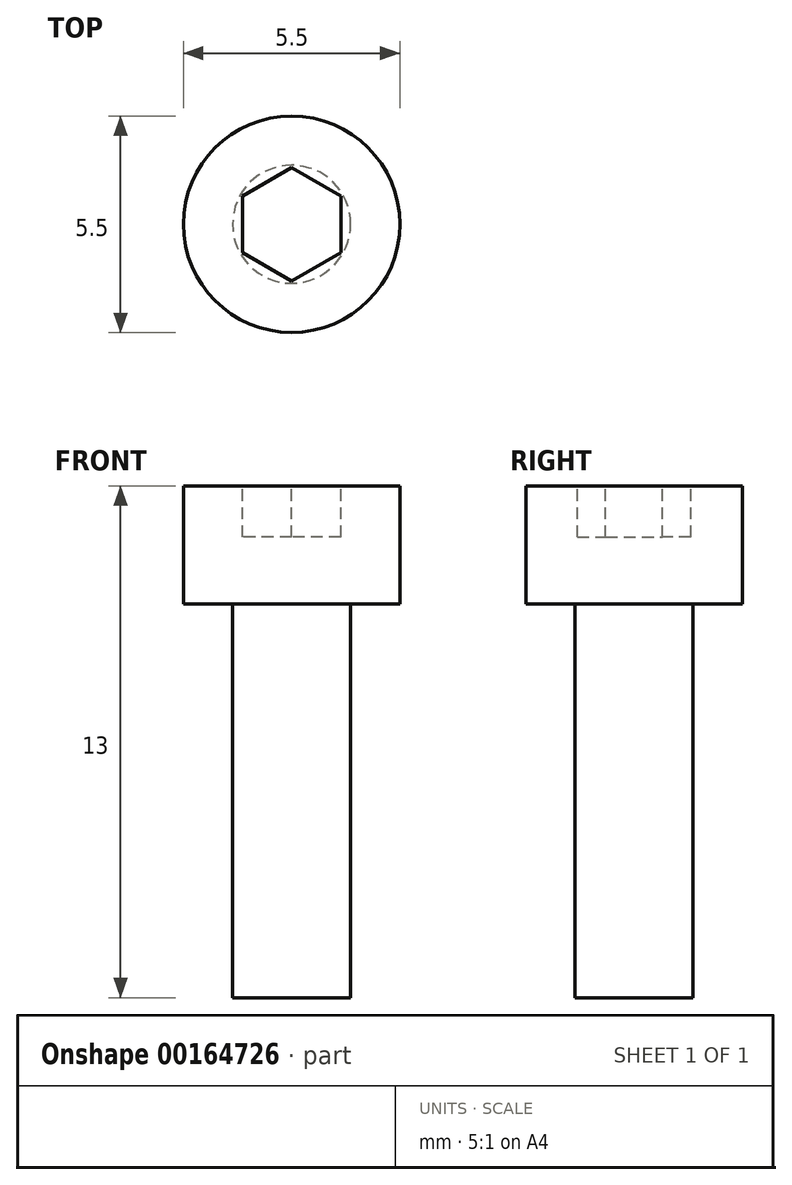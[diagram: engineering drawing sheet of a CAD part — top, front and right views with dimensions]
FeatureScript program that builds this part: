
annotation { "Feature Type Name" : "Feature", "Feature Type Description" : "" }
export const myFeature = defineFeature(function(context is Context, id is Id, definition is map)
    precondition{}
    {
        {
            var Q0;
            Q0=qCreatedBy(makeId("Front.planeOp"),FACE);
            var sketch = newSketch(context, id + "F0", { "sketchPlane" : qUnion([Q0])});
            skLineSegment(sketch, "E0", {"start": v(-1.5, 0) * mm, "end": v(-2.75, 0) * mm});
            skLineSegment(sketch, "E1", {"start": v(-2.75, 0) * mm, "end": v(-2.75, 3) * mm});
            skLineSegment(sketch, "E2", {"start": v(-2.75, 3) * mm, "end": v(0, 3) * mm});
            skLineSegment(sketch, "E3", {"start": v(0, 3) * mm, "end": v(0, 0) * mm});
            skLineSegment(sketch, "E4", {"start": v(-1.5, 0) * mm, "end": v(-1.5, -10) * mm});
            skLineSegment(sketch, "E5", {"start": v(-1.5, -10) * mm, "end": v(0, -10) * mm});
            skLineSegment(sketch, "E6", {"start": v(0, -10) * mm, "end": v(0, 0) * mm});
            skLineSegment(sketch, "E7", {"start": v(0, 3) * mm, "end": v(0, 8.62) * mm, "construction": true});
            skSolve(sketch);
        }
        {
            var Q0;
            Q0=makeQuery(id+"F0.imprint","IMPRINT",FACE,{"disambiguationData":[TD([[makeQuery(id+"F0.imprint","IMPRINT",EDGE,{"derivedFrom":sQuery(id+"F0.wireOp",EDGE,"E0")}),-1.0]])]});
            var Q1;
            Q1=sQuery(id+"F0.wireOp",EDGE,"E6");
            revolve(context, id + "F1", {"entities" : qUnion([Q0]), "axis" : qUnion([Q1]), "revolveType" : RevolveType.FULL});
        }
        {
            var Q0;
            Q0=makeQuery(id+"F1.opRevolve","SWEPT_FACE",FACE,{"disambiguationData":[OSD([sQuery(id+"F0.wireOp",EDGE,"E2")])]});
            var sketch = newSketch(context, id + "F2", { "sketchPlane" : qUnion([Q0])});
            skCircle(sketch, "E8.cCircle", {"center": v(0, 0) * mm, "radius": 1.25 * mm, "construction": true});
            skLineSegment(sketch, "E8.0", {"start": v(-1.25, -0.72) * mm, "end": v(-1.25, 0.72) * mm});
            skLineSegment(sketch, "E8.1", {"start": v(-1.25, 0.72) * mm, "end": v(0, 1.44) * mm});
            skLineSegment(sketch, "E8.2", {"start": v(0, 1.44) * mm, "end": v(1.25, 0.72) * mm});
            skLineSegment(sketch, "E8.3", {"start": v(1.25, 0.72) * mm, "end": v(1.25, -0.72) * mm});
            skLineSegment(sketch, "E8.4", {"start": v(1.25, -0.72) * mm, "end": v(0, -1.44) * mm});
            skLineSegment(sketch, "E8.5", {"start": v(0, -1.44) * mm, "end": v(-1.25, -0.72) * mm});
            skPoint(sketch, "E8.0.midPoint", {"position": v(-1.25, 0) * mm});
            skSolve(sketch);
        }
        {
            var Q0;
            Q0=qSketchRegion(id+"F2",true);
            extrude(context, id + "F3", {"entities" : qUnion([Q0]), "operationType" : NewBodyOperationType.REMOVE, "oppositeDirection" : true, "depth" : 1.3 * mm});
        }
    });
